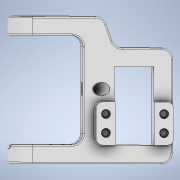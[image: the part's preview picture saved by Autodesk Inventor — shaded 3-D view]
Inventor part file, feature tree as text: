
AUTODESK INVENTOR PART (.ipt)
format: ipt  version: 2020.3 (Build 243373000, 373)  size: 541,184 bytes
history: native  units: mm
features: fillet x11, sketch x8, extrude x6, hole x5, plane x2, chamfer x1
ambient origin geometry x8: Origin, YZ Plane, XZ Plane, XY Plane, X Axis, Y Axis, Z Axis, Center Point
bodies: Solid1 (feature_tree)
feature tree (33):
  sketch  "Sketch1"  dims[d4=24.6mm d5=12.4mm]
  extrude  "Extrusion1"  Depth=12.4mm
  hole  "Hole1"  [1 undecoded]
  fillet  "Fillet1"  Radius=23.5mm
  fillet  "Fillet2"  Radius=34.5mm
  sketch  "Sketch2"  dims[d9=6.0mm d11=10.0mm d12=23.5mm d14=34.5mm]
  hole  "Hole2"  [1 undecoded]
  sketch  "Sketch8"  dims[d19=1.9mm d20=6.0mm d21=4.0mm d22=2.0mm d23=90.0deg d24=10.0mm d25=20.594885mm]
  extrude  "Extrusion3"  Depth=6.0mm
  extrude  "Extrusion4"  Depth=3.7mm
  hole  "Hole5"  [1 undecoded]
  fillet  "Fillet4"  Radius=10.0mm
  fillet  "Fillet9"  Radius=3.5mm
  fillet  "Fillet10"  Radius=0.5mm
  fillet  "Fillet5"  Radius=0.5mm
  fillet  "Fillet6"  Radius=28.4mm
  hole  "Hole4"  [1 undecoded]
  fillet  "Fillet11"  Radius=6.0mm
  extrude  "Extrusion6"  Depth=2.0mm
  plane  "Work Plane1"
  extrude  "Extrusion7"  Depth=0.5mm
  fillet  "Fillet12"  Radius=2.0mm
  hole  "Hole6"  [1 undecoded]
  plane  "Work Plane3"
  extrude  "Extrusion8"  Depth=2.0mm
  chamfer  "Chamfer1"  Distance=0.3mm
  fillet  "Fillet13"  Radius=0.2mm
  fillet  "Fillet14"  [1 undecoded]
  sketch  "Sketch3"  dims[d16=6.0mm d17=15.0mm d18=0.0mm]
  sketch  "Sketch9"  dims[d27=8.8mm d28=6.0mm d29=4.0mm d30=2.0mm d31=90.0deg d32=8.0mm d33=20.594885mm d34=6.0mm]
  sketch  "Sketch10"  dims[d37=7.2mm d38=3.7mm]
  sketch  "Sketch11"  dims[d39=12.1mm d40=3.5mm d41=0.0mm d42=10.0mm d43=0.0mm d53=3.5mm d54=0.5mm d55=0.5mm d57=28.4mm]
  sketch  "Sketch12"  dims[d58=6.8mm d59=20.92mm d60=0.0mm d61=6.0mm d62=3.0mm d63=6.0mm d64=4.0mm d65=2.0mm d66=90.0deg d67=4.3mm d68=0.0mm d70=2.0mm d71=0.5mm d72=2.0mm d74=2.0mm d75=2.0mm d76=1.0mm d77=6.0mm d78=4.0mm d79=2.0mm d80=90.0deg d81=8.0mm d82=20.594885mm d83=0.3mm d84=0.2mm d85=0.0mm d86=0.0mm d87=1.0mm d88=3.5mm d89=-9.075712mm d90=4.0mm d91=4.0mm d92=1.0mm d93=33.941mm d94=0.0mm d95=0.2mm d96=2.1mm d97=6.0mm d98=4.0mm d99=2.0mm d100=90.0deg d101=7.3mm d102=0.0mm d103=24.0mm d104=7.0mm d105=7.0mm d106=0.0mm d107=0.2mm d108=0.8mm d109=45.0deg d110=1.0mm d111=2.0mm d112=3.490659mm]
note: 6 required parameter values undecoded (feature->parameter linkage not recoverable at this tier; creation-order binding heuristic only, values carry confidence <= 0.55)
